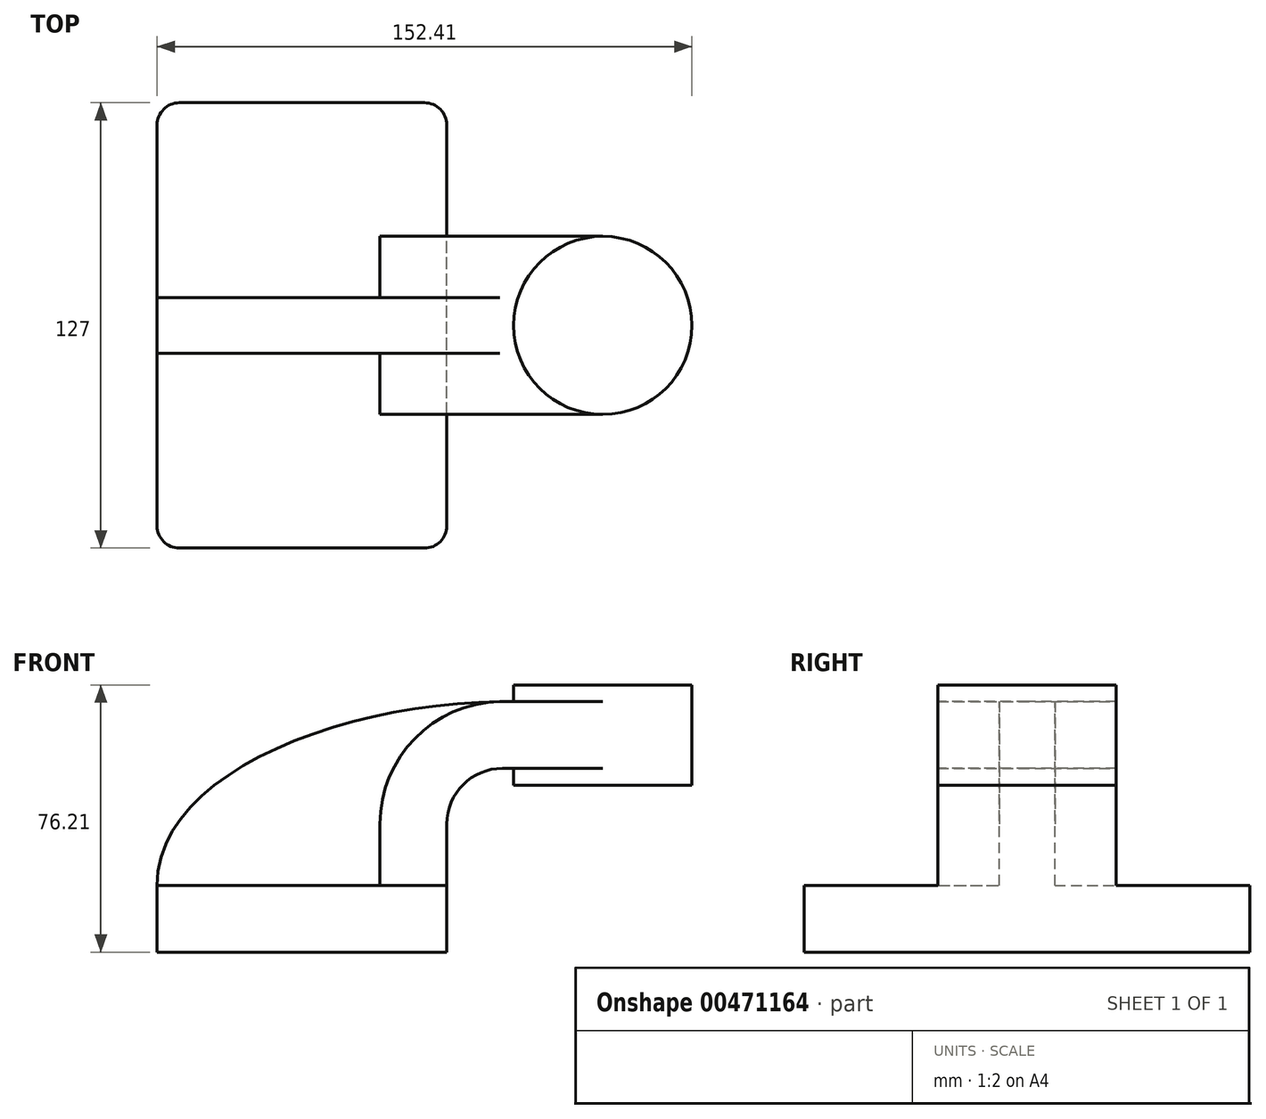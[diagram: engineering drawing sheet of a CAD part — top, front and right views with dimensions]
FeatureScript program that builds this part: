
annotation { "Feature Type Name" : "Feature", "Feature Type Description" : "" }
export const myFeature = defineFeature(function(context is Context, id is Id, definition is map)
    precondition{}
    {
        {
            var Q0;
            Q0=qCreatedBy(makeId("Front.planeOp"),FACE);
            var sketch = newSketch(context, id + "F0", { "sketchPlane" : qUnion([Q0])});
            skLineSegment(sketch, "E0.bottom", {"start": v(41.28, -9.52) * mm, "end": v(-41.28, -9.53) * mm});
            skLineSegment(sketch, "E0.top", {"start": v(41.28, 9.53) * mm, "end": v(-41.28, 9.53) * mm});
            skLineSegment(sketch, "E0.left", {"start": v(41.28, -9.52) * mm, "end": v(41.28, 9.53) * mm});
            skLineSegment(sketch, "E0.right", {"start": v(-41.28, -9.53) * mm, "end": v(-41.28, 9.53) * mm});
            skPoint(sketch, "E0.middle", {"position": v(0, 0) * mm});
            skLineSegment(sketch, "E1", {"start": v(41.28, 9.53) * mm, "end": v(41.28, 27) * mm});
            skArc(sketch, "E2", {"start": v(41.27, 27) * mm, "mid": v(45.92, 38.23) * mm, "end": v(57.15, 42.88) * mm});
            skLineSegment(sketch, "E3.bottom", {"start": v(111.13, 38.1) * mm, "end": v(60.33, 38.1) * mm});
            skLineSegment(sketch, "E3.top", {"start": v(111.12, 66.68) * mm, "end": v(60.33, 66.68) * mm});
            skLineSegment(sketch, "E3.left", {"start": v(111.12, 38.1) * mm, "end": v(111.12, 66.68) * mm});
            skLineSegment(sketch, "E3.right", {"start": v(60.33, 38.1) * mm, "end": v(60.33, 66.68) * mm});
            skPoint(sketch, "E3.middle", {"position": v(85.73, 52.39) * mm});
            skLineSegment(sketch, "E4", {"start": v(57.15, 42.88) * mm, "end": v(85.73, 42.88) * mm});
            skPoint(sketch, "E4.endSnap0", {"position": v(85.73, 38.1) * mm});
            skLineSegment(sketch, "E5.0", {"start": v(57.15, 61.93) * mm, "end": v(85.73, 61.93) * mm});
            skArc(sketch, "E5.1", {"start": v(22.23, 27) * mm, "mid": v(32.45, 51.7) * mm, "end": v(57.15, 61.93) * mm});
            skLineSegment(sketch, "E5.2", {"start": v(22.22, 9.53) * mm, "end": v(22.22, 27) * mm});
            skLineSegment(sketch, "E6", {"start": v(85.72, 38.1) * mm, "end": v(85.72, 66.68) * mm});
            skFitSpline(sketch, "E7", {"points": [v(-41.28, 9.52) * mm, v(57.15, 61.93) * mm], "startDerivative": vector(-0.5, 95.28) * mm, "endDerivative": vector(138.58, 1.19) * mm});
            skSolve(sketch);
        }
        {
            var Q0;
            Q0=makeQuery(id+"F0.imprint","IMPRINT",FACE,{"disambiguationData":[TD([[makeQuery(id+"F0.imprint","IMPRINT",EDGE,{"derivedFrom":sQuery(id+"F0.wireOp",EDGE,"E0.bottom")}),-1.0]])]});
            extrude(context, id + "F1", {"entities" : qUnion([Q0]), "endBound" : BoundingType.SYMMETRIC, "depth" : 127 * mm});
        }
        {
            var Q0;
            {var subQ0=sQuery(id+"F0.wireOp",EDGE,"E4");var subQ1=sQuery(id+"F0.wireOp",EDGE,"E3.right");var subQ2=makeQuery(id+"F0.imprint","INTERSECT",VERTEX,{"derivedFrom":[subQ1,subQ0]});Q0=makeQuery(id+"F0.imprint","IMPRINT",FACE,{"disambiguationData":[TD([[makeQuery(id+"F0.imprint","IMPRINT",EDGE,{"disambiguationData":[TD([[subQ2,-1.0]])],"derivedFrom":subQ1}),-1.0]])]});}
            var Q1;
            {var subQ5=sQuery(id+"F0.wireOp",EDGE,"E1");Q1=makeQuery(id+"F0.imprint","IMPRINT",FACE,{"disambiguationData":[TD([[makeQuery(id+"F0.imprint","IMPRINT",EDGE,{"derivedFrom":subQ5}),1.0]])]});}
            extrude(context, id + "F2", {"entities" : qUnion([Q0, Q1]), "operationType" : NewBodyOperationType.ADD, "endBound" : BoundingType.SYMMETRIC, "depth" : 50.8 * mm});
        }
        {
            var Q0;
            {var subQ3=sQuery(id+"F0.wireOp",EDGE,"E5.2");Q0=makeQuery(id+"F0.imprint","IMPRINT",FACE,{"disambiguationData":[TD([[makeQuery(id+"F0.imprint","IMPRINT",EDGE,{"derivedFrom":subQ3}),1.0]])]});}
            extrude(context, id + "F3", {"entities" : qUnion([Q0]), "operationType" : NewBodyOperationType.ADD, "endBound" : BoundingType.SYMMETRIC, "depth" : 15.88 * mm});
        }
        {
            var Q0;
            {var subQ0=sQuery(id+"F0.wireOp",EDGE,"E3.left");Q0=makeQuery(id+"F0.imprint","IMPRINT",FACE,{"disambiguationData":[TD([[makeQuery(id+"F0.imprint","IMPRINT",EDGE,{"derivedFrom":subQ0}),1.0]])]});}
            var Q1;
            Q1=sQuery(id+"F0.wireOp",EDGE,"E6");
            revolve(context, id + "F4", {"operationType" : NewBodyOperationType.ADD, "entities" : qUnion([Q0]), "axis" : qUnion([Q1]), "revolveType" : RevolveType.FULL});
        }
        {
            var Q0;
            Q0=makeQuery(id+"F1.opExtrude","CAP_EDGE",EDGE,{"disambiguationData":[OSD([sQuery(id+"F0.wireOp",EDGE,"E0.left")])],"isStart":false});
            var Q1;
            Q1=makeQuery(id+"F1.opExtrude","CAP_EDGE",EDGE,{"disambiguationData":[OSD([sQuery(id+"F0.wireOp",EDGE,"E0.right")])],"isStart":false});
            var Q2;
            Q2=makeQuery(id+"F1.opExtrude","CAP_EDGE",EDGE,{"disambiguationData":[OSD([sQuery(id+"F0.wireOp",EDGE,"E0.left")])],"isStart":true});
            var Q3;
            Q3=makeQuery(id+"F1.opExtrude","CAP_EDGE",EDGE,{"disambiguationData":[OSD([sQuery(id+"F0.wireOp",EDGE,"E0.right")])],"isStart":true});
            fillet(context, id + "F5", {"entities" : qUnion([Q0, Q1, Q2, Q3]), "radius" : 6.35 * mm, "tangentPropagation" : true, "allowEdgeOverflow" : false});
        }
    });
